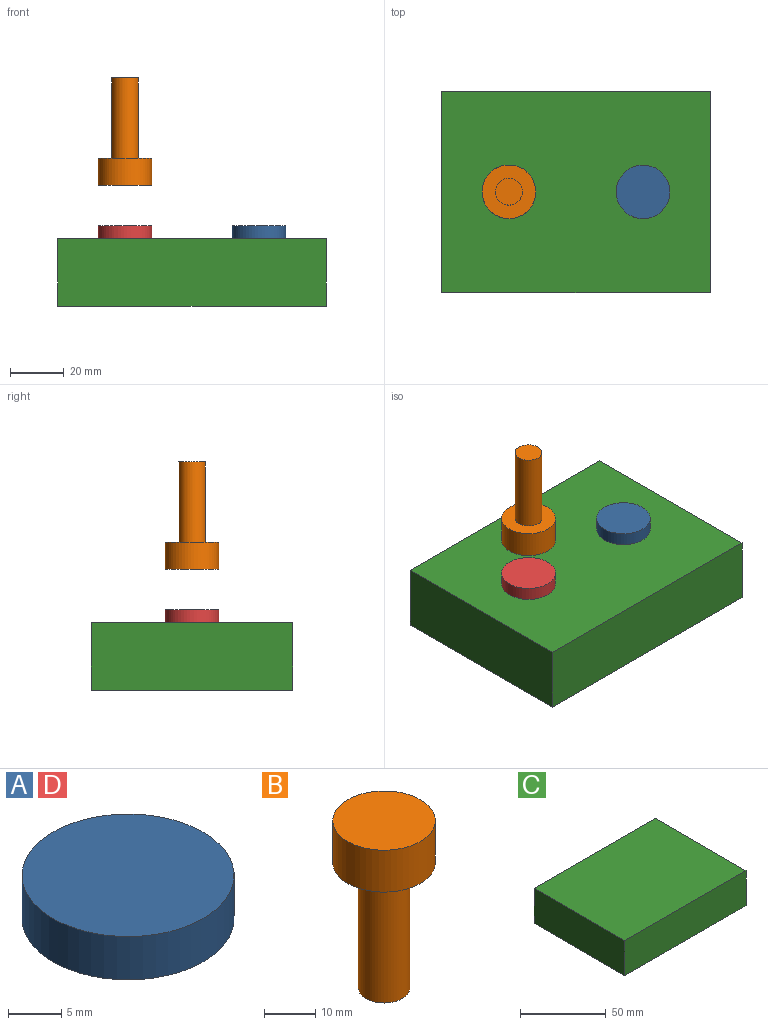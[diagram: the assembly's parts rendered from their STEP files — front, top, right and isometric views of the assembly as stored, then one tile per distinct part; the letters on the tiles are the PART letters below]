
ASSEMBLY  parts=4 mates=4
PART A: 3 faces, bbox 20x20x5 mm
  f0: cylinder r=10mm len=20mm, axis (0,0,-1), area 314.2mm2, adj f1,f2
  f1: plane 20x20mm, normal (0,0,1), area 314.2mm2, adj f0
  f2: plane 20x20mm, normal (0,0,-1), area 314.2mm2, adj f0
PART B: 5 faces, bbox 20x20x40 mm
  f0: plane 10x10mm, normal (0,0,-1), area 78.5mm2, adj f1
  f1: cylinder r=5mm len=30mm, axis (0,0,1), area 942.5mm2, adj f0,f2
  f2: plane 20x20mm, normal (0,0,-1), area 235.6mm2, adj f1,f3
  f3: cylinder r=10mm len=20mm, axis (0,0,1), area 628.3mm2, adj f2,f4
  f4: plane 20x20mm, normal (0,0,1), area 314.2mm2, adj f3
PART C: 6 faces, bbox 100x75x25 mm
  f0: plane 75x25mm, normal (-1,0,0), area 1875mm2, adj f1,f3,f4,f5
  f1: plane 100x25mm, normal (0,-1,0), area 2500mm2, adj f0,f2,f4,f5
  f2: plane 75x25mm, normal (1,0,0), area 1875mm2, adj f1,f3,f4,f5
  f3: plane 100x25mm, normal (0,1,0), area 2500mm2, adj f0,f2,f4,f5
  f4: plane 100x75mm, normal (0,0,1), area 7500mm2, adj f0,f1,f2,f3
  f5: plane 100x75mm, normal (0,0,-1), area 7500mm2, adj f0,f1,f2,f3
PART D: same geometry as A
PLACE A rot(axis=(1,0,0),180deg) t=(78.39,41.81,33.98)mm
PLACE B rot(axis=(0.71,-0.71,0),180deg) t=(28.39,41.81,88.98)mm
PLACE C t=(3.39,4.31,3.98)mm fixed
PLACE D rot(axis=(1,0,0),180deg) t=(28.39,41.81,33.98)mm
MATE planar A.f0 <-> C.f4  axis (0,0,-1) through (78.39,41.81,28.98)mm
MATE slider A.f0 <-> C.f4  axis (0,0,-1) through (78.39,41.81,28.98)mm
MATE planar D.f0 <-> B.f1  axis (0,0,1) through (28.39,41.81,33.98)mm
MATE cylindrical B.f1 <-> D.f0  axis (0,0,-1) through (28.39,41.81,48.98)mm
